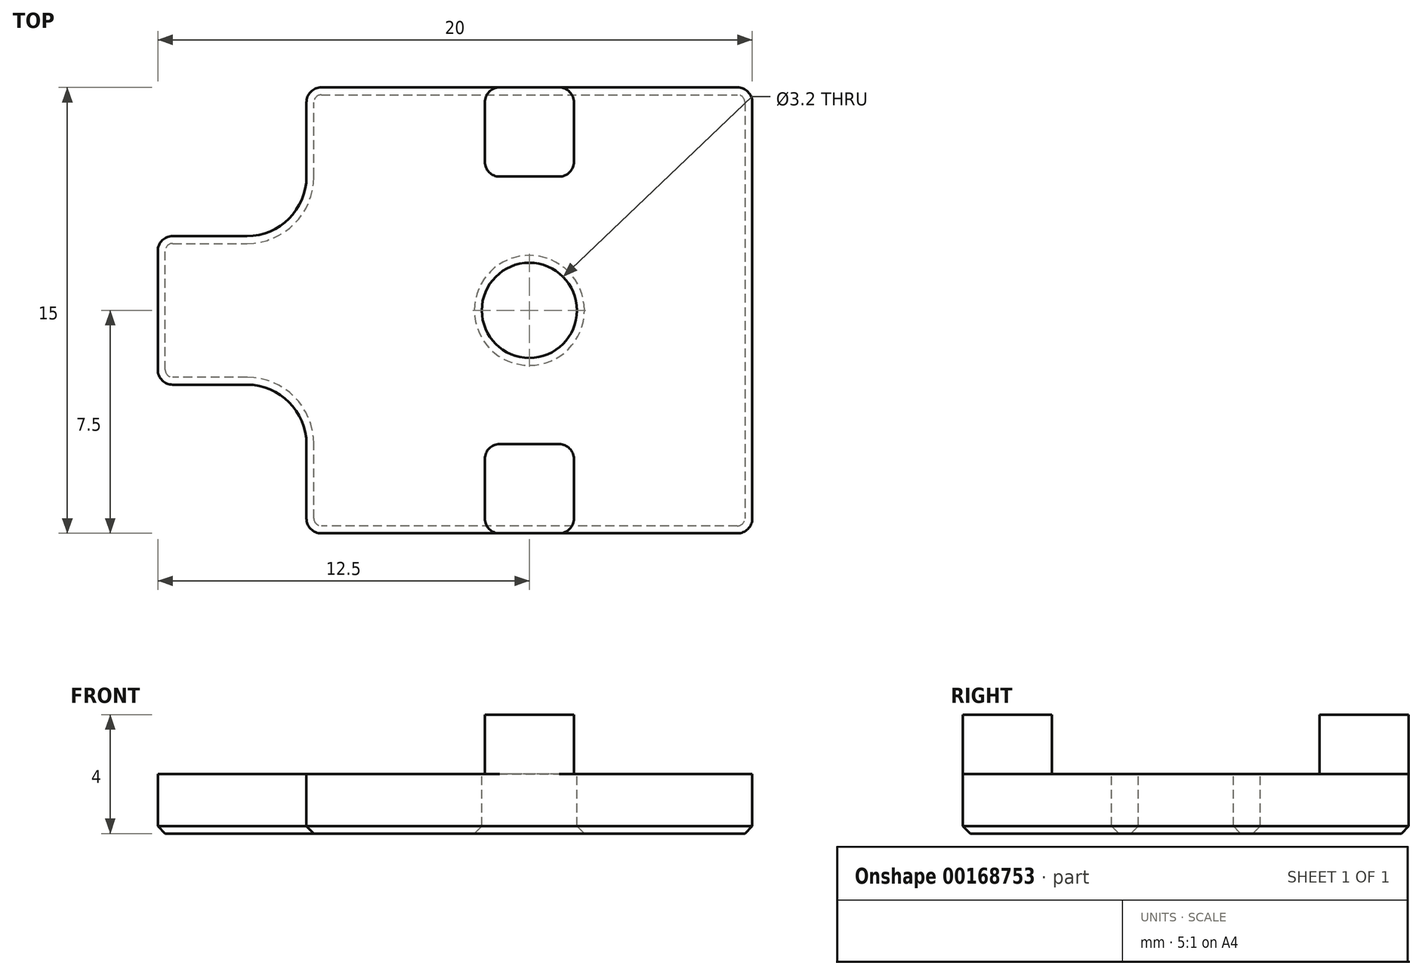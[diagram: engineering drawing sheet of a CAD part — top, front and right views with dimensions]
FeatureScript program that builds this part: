
annotation { "Feature Type Name" : "Feature", "Feature Type Description" : "" }
export const myFeature = defineFeature(function(context is Context, id is Id, definition is map)
    precondition{}
    {
        {
            var Q0;
            Q0=qCreatedBy(makeId("Top.planeOp"),FACE);
            var sketch = newSketch(context, id + "F0", { "sketchPlane" : qUnion([Q0])});
            skLineSegment(sketch, "E0.bottom", {"start": v(7.5, 7.5) * mm, "end": v(-7.5, 7.5) * mm});
            skLineSegment(sketch, "E0.top", {"start": v(7.5, -7.5) * mm, "end": v(-7.5, -7.5) * mm});
            skLineSegment(sketch, "E0.left", {"start": v(7.5, 7.5) * mm, "end": v(7.5, -7.5) * mm});
            skLineSegment(sketch, "E0.right", {"start": v(-7.5, 7.5) * mm, "end": v(-7.5, -7.5) * mm});
            skPoint(sketch, "E0.middle", {"position": v(0, 0) * mm});
            skLineSegment(sketch, "E1", {"start": v(-7.5, 2.5) * mm, "end": v(-12.5, 2.5) * mm});
            skLineSegment(sketch, "E2", {"start": v(-12.5, 2.5) * mm, "end": v(-12.5, -2.5) * mm});
            skLineSegment(sketch, "E3", {"start": v(-12.5, -2.5) * mm, "end": v(-7.5, -2.5) * mm});
            skCircle(sketch, "E4", {"center": v(0, 0) * mm, "radius": 1.6 * mm});
            skLineSegment(sketch, "E5.top", {"start": v(1.5, 4.5) * mm, "end": v(-1.5, 4.5) * mm});
            skLineSegment(sketch, "E5.left", {"start": v(1.5, 7.5) * mm, "end": v(1.5, 4.5) * mm});
            skLineSegment(sketch, "E5.right", {"start": v(-1.5, 7.5) * mm, "end": v(-1.5, 4.5) * mm});
            skPoint(sketch, "E5.middle", {"position": v(0, 6) * mm});
            skLineSegment(sketch, "E6.MirrorCS", {"start": v(-1.5, -7.5) * mm, "end": v(-1.5, -4.5) * mm});
            skLineSegment(sketch, "E7.MirrorCS", {"start": v(1.5, -4.5) * mm, "end": v(-1.5, -4.5) * mm});
            skLineSegment(sketch, "E8.MirrorCS", {"start": v(1.5, -7.5) * mm, "end": v(1.5, -4.5) * mm});
            skSolve(sketch);
        }
        {
            var Q0;
            {var subQ1=sQuery(id+"F0.wireOp",EDGE,"E0.bottom");Q0=makeQuery(id+"F0.imprint","IMPRINT",FACE,{"disambiguationData":[TD([[makeQuery(id+"F0.imprint","IMPRINT",EDGE,{"derivedFrom":subQ1}),1.0]])]});}
            var Q1;
            {var subQ0=sQuery(id+"F0.wireOp",EDGE,"E1");Q1=makeQuery(id+"F0.imprint","IMPRINT",FACE,{"disambiguationData":[TD([[makeQuery(id+"F0.imprint","IMPRINT",EDGE,{"derivedFrom":subQ0}),1.0]])]});}
            var Q2;
            Q2=makeQuery(id+"F0.imprint","IMPRINT",FACE,{"disambiguationData":[TD([[makeQuery(id+"F0.imprint","IMPRINT",EDGE,{"derivedFrom":sQuery(id+"F0.wireOp",EDGE,"E5.top")}),-1.0]])]});
            var Q3;
            {var subQ0=sQuery(id+"F0.wireOp",EDGE,"E6.MirrorCS");Q3=makeQuery(id+"F0.imprint","IMPRINT",FACE,{"disambiguationData":[TD([[makeQuery(id+"F0.imprint","IMPRINT",EDGE,{"derivedFrom":subQ0}),-1.0]])]});}
            extrude(context, id + "F1", {"entities" : qUnion([Q0, Q1, Q2, Q3]), "oppositeDirection" : true, "depth" : 2 * mm});
        }
        {
            var Q0;
            Q0=makeQuery(id+"F0.imprint","IMPRINT",FACE,{"disambiguationData":[TD([[makeQuery(id+"F0.imprint","IMPRINT",EDGE,{"derivedFrom":sQuery(id+"F0.wireOp",EDGE,"E5.top")}),-1.0]])]});
            var Q1;
            {var subQ0=sQuery(id+"F0.wireOp",EDGE,"E6.MirrorCS");Q1=makeQuery(id+"F0.imprint","IMPRINT",FACE,{"disambiguationData":[TD([[makeQuery(id+"F0.imprint","IMPRINT",EDGE,{"derivedFrom":subQ0}),-1.0]])]});}
            extrude(context, id + "F2", {"entities" : qUnion([Q0, Q1]), "operationType" : NewBodyOperationType.ADD, "depth" : 2 * mm});
        }
        {
            var Q0;
            Q0=makeQuery(id+"F1.opExtrude","SWEPT_EDGE",EDGE,{"disambiguationData":[OSD([sQuery(id+"F0.wireOp",EDGE,"E0.right"),sQuery(id+"F0.wireOp",EDGE,"E1")])]});
            var Q1;
            Q1=makeQuery(id+"F1.opExtrude","SWEPT_EDGE",EDGE,{"disambiguationData":[OSD([sQuery(id+"F0.wireOp",EDGE,"E0.right"),sQuery(id+"F0.wireOp",EDGE,"E3")])]});
            fillet(context, id + "F3", {"entities" : qUnion([Q0, Q1]), "radius" : 2 * mm, "allowEdgeOverflow" : false});
        }
        {
            var Q0;
            Q0=makeQuery(id+"F1.opExtrude","SWEPT_EDGE",EDGE,{"disambiguationData":[OSD([sQuery(id+"F0.wireOp",EDGE,"E1"),sQuery(id+"F0.wireOp",EDGE,"E2")])]});
            var Q1;
            Q1=makeQuery(id+"F1.opExtrude","SWEPT_EDGE",EDGE,{"disambiguationData":[OSD([sQuery(id+"F0.wireOp",EDGE,"E2"),sQuery(id+"F0.wireOp",EDGE,"E3")])]});
            var Q2;
            Q2=makeQuery(id+"F1.opExtrude","SWEPT_EDGE",EDGE,{"disambiguationData":[OSD([sQuery(id+"F0.wireOp",EDGE,"E0.top"),sQuery(id+"F0.wireOp",EDGE,"E0.right")])]});
            var Q3;
            Q3=makeQuery(id+"F1.opExtrude","SWEPT_EDGE",EDGE,{"disambiguationData":[OSD([sQuery(id+"F0.wireOp",EDGE,"E0.bottom"),sQuery(id+"F0.wireOp",EDGE,"E0.right")])]});
            var Q4;
            Q4=makeQuery(id+"F1.opExtrude","SWEPT_EDGE",EDGE,{"disambiguationData":[OSD([sQuery(id+"F0.wireOp",EDGE,"E0.bottom"),sQuery(id+"F0.wireOp",EDGE,"E0.left")])]});
            var Q5;
            Q5=makeQuery(id+"F1.opExtrude","SWEPT_EDGE",EDGE,{"disambiguationData":[OSD([sQuery(id+"F0.wireOp",EDGE,"E0.top"),sQuery(id+"F0.wireOp",EDGE,"E0.left")])]});
            var Q6;
            Q6=makeQuery(id+"F2.opExtrude","SWEPT_EDGE",EDGE,{"disambiguationData":[OSD([sQuery(id+"F0.wireOp",EDGE,"E0.bottom"),sQuery(id+"F0.wireOp",EDGE,"E5.left")])]});
            var Q7;
            Q7=makeQuery(id+"F2.opExtrude","SWEPT_EDGE",EDGE,{"disambiguationData":[OSD([sQuery(id+"F0.wireOp",EDGE,"E5.top"),sQuery(id+"F0.wireOp",EDGE,"E5.left")])]});
            var Q8;
            Q8=makeQuery(id+"F2.opExtrude","SWEPT_EDGE",EDGE,{"disambiguationData":[OSD([sQuery(id+"F0.wireOp",EDGE,"E0.bottom"),sQuery(id+"F0.wireOp",EDGE,"E5.right")])]});
            var Q9;
            Q9=makeQuery(id+"F2.opExtrude","SWEPT_EDGE",EDGE,{"disambiguationData":[OSD([sQuery(id+"F0.wireOp",EDGE,"E5.top"),sQuery(id+"F0.wireOp",EDGE,"E5.right")])]});
            var Q10;
            Q10=makeQuery(id+"F2.opExtrude","SWEPT_EDGE",EDGE,{"disambiguationData":[OSD([sQuery(id+"F0.wireOp",EDGE,"E6.MirrorCS"),sQuery(id+"F0.wireOp",EDGE,"E7.MirrorCS")])]});
            var Q11;
            Q11=makeQuery(id+"F2.opExtrude","SWEPT_EDGE",EDGE,{"disambiguationData":[OSD([sQuery(id+"F0.wireOp",EDGE,"E7.MirrorCS"),sQuery(id+"F0.wireOp",EDGE,"E8.MirrorCS")])]});
            var Q12;
            Q12=makeQuery(id+"F2.opExtrude","SWEPT_EDGE",EDGE,{"disambiguationData":[OSD([sQuery(id+"F0.wireOp",EDGE,"E0.top"),sQuery(id+"F0.wireOp",EDGE,"E6.MirrorCS")])]});
            var Q13;
            Q13=makeQuery(id+"F2.opExtrude","SWEPT_EDGE",EDGE,{"disambiguationData":[OSD([sQuery(id+"F0.wireOp",EDGE,"E0.top"),sQuery(id+"F0.wireOp",EDGE,"E8.MirrorCS")])]});
            fillet(context, id + "F4", {"entities" : qUnion([Q0, Q1, Q2, Q3, Q4, Q5, Q6, Q7, Q8, Q9, Q10, Q11, Q12, Q13]), "radius" : 0.5 * mm, "allowEdgeOverflow" : false});
        }
        {
            var Q0;
            Q0=makeQuery(id+"F1.opExtrude","CAP_FACE",FACE,{"disambiguationData":[OSD([sQuery(id+"F0.wireOp",EDGE,"E0.bottom"),sQuery(id+"F0.wireOp",EDGE,"E0.top"),sQuery(id+"F0.wireOp",EDGE,"E0.left"),sQuery(id+"F0.wireOp",EDGE,"E0.right"),sQuery(id+"F0.wireOp",EDGE,"E1"),sQuery(id+"F0.wireOp",EDGE,"E2"),sQuery(id+"F0.wireOp",EDGE,"E3"),sQuery(id+"F0.wireOp",EDGE,"E4")])],"isStart":false});
            chamfer(context, id + "F5", {"entities" : qUnion([Q0]), "width" : 0.25 * mm});
        }
    });
